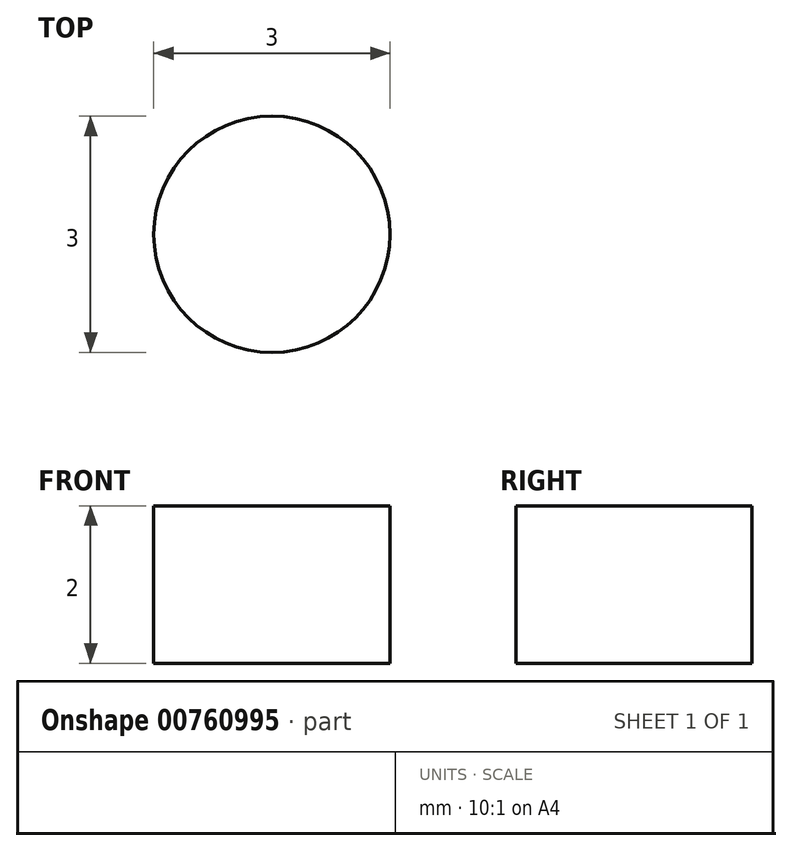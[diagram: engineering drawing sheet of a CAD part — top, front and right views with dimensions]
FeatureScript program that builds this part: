
annotation { "Feature Type Name" : "Feature", "Feature Type Description" : "" }
export const myFeature = defineFeature(function(context is Context, id is Id, definition is map)
    precondition{}
    {
        {
            var Q0;
            Q0=qCreatedBy(makeId("Top.planeOp"),FACE);
            var sketch = newSketch(context, id + "F0", { "sketchPlane" : qUnion([Q0])});
            skCircle(sketch, "E0", {"center": v(0, 0) * mm, "radius": 1.5 * mm});
            skSolve(sketch);
        }
        {
            var Q0;
            Q0 = qSketchRegion(id + "F0", true);
            extrude(context, id + "F1", {"entities" : qUnion([Q0]), "depth" : 2 * mm, "offsetDistance" : 25 * mm});
        }
    });
